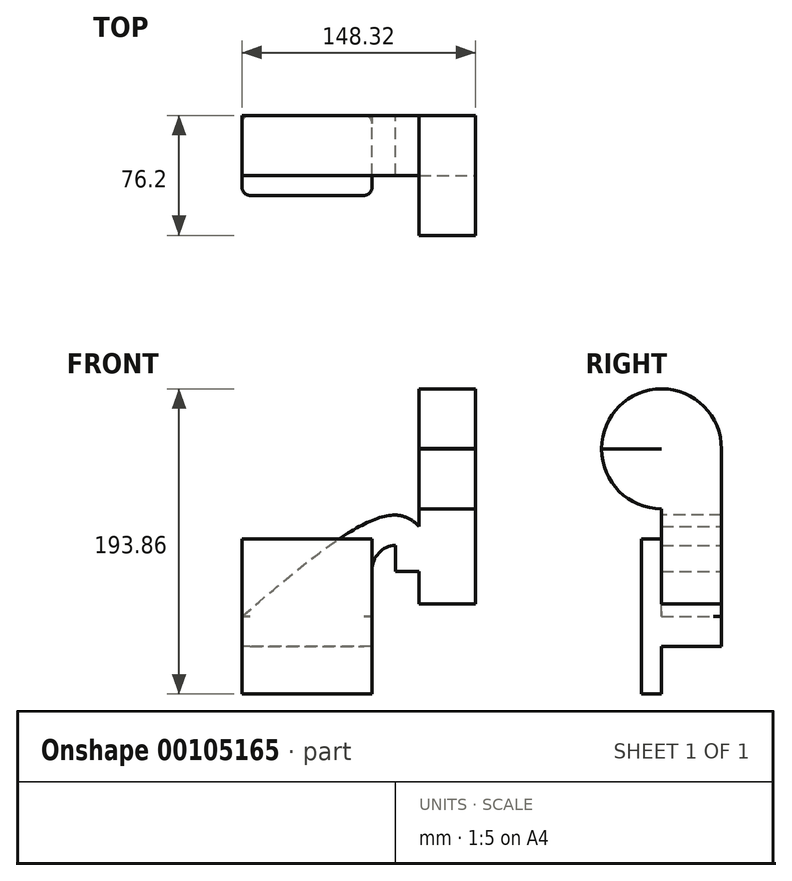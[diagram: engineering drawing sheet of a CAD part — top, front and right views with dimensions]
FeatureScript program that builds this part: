
annotation { "Feature Type Name" : "Feature", "Feature Type Description" : "" }
export const myFeature = defineFeature(function(context is Context, id is Id, definition is map)
    precondition{}
    {
        {
            var Q0;
            Q0=qCreatedBy(makeId("Front.planeOp"),FACE);
            var sketch = newSketch(context, id + "F0", { "sketchPlane" : qUnion([Q0])});
            skLineSegment(sketch, "E0.bottom", {"start": v(-41.28, 9.52) * mm, "end": v(41.27, 9.53) * mm});
            skLineSegment(sketch, "E0.top", {"start": v(-41.28, -9.53) * mm, "end": v(41.28, -9.53) * mm});
            skLineSegment(sketch, "E0.left", {"start": v(-41.28, 9.52) * mm, "end": v(-41.27, -9.53) * mm});
            skLineSegment(sketch, "E0.right", {"start": v(41.28, 9.53) * mm, "end": v(41.28, -9.52) * mm});
            skPoint(sketch, "E0.middle", {"position": v(0, 0) * mm});
            skLineSegment(sketch, "E1.bottom", {"start": v(56.24, 66.67) * mm, "end": v(107.04, 66.67) * mm});
            skLineSegment(sketch, "E1.top", {"start": v(56.24, 38.1) * mm, "end": v(107.04, 38.1) * mm});
            skLineSegment(sketch, "E1.left", {"start": v(56.24, 66.67) * mm, "end": v(56.24, 38.1) * mm});
            skLineSegment(sketch, "E1.right", {"start": v(107.04, 66.67) * mm, "end": v(107.04, 38.1) * mm});
            skPoint(sketch, "E1.middle", {"position": v(81.64, 52.39) * mm});
            skLineSegment(sketch, "E2", {"start": v(41.27, 9.53) * mm, "end": v(41.27, 38.94) * mm});
            skArc(sketch, "E3", {"start": v(41.27, 38.94) * mm, "mid": v(45.92, 50.17) * mm, "end": v(57.15, 54.81) * mm});
            skLineSegment(sketch, "E4", {"start": v(57.15, 54.81) * mm, "end": v(101.6, 54.81) * mm});
            skArc(sketch, "E5.0", {"start": v(22.22, 38.94) * mm, "mid": v(32.45, 63.64) * mm, "end": v(57.15, 73.86) * mm});
            skLineSegment(sketch, "E5.1", {"start": v(22.22, 9.53) * mm, "end": v(22.22, 38.94) * mm});
            skLineSegment(sketch, "E6", {"start": v(57.15, 54.81) * mm, "end": v(57.15, 73.86) * mm});
            skFitSpline(sketch, "E7", {"points": [v(-41.28, 9.52) * mm, v(57.15, 73.86) * mm, v(81.64, 52.39) * mm], "startDerivative": vector(176.18, 150.78) * mm, "endDerivative": vector(57.36, -89.95) * mm});
            skSolve(sketch);
        }
        {
            var Q0;
            Q0=makeQuery(id+"F0.imprint","IMPRINT",FACE,{"disambiguationData":[TD([[makeQuery(id+"F0.imprint","IMPRINT",EDGE,{"derivedFrom":sQuery(id+"F0.wireOp",EDGE,"E0.top")}),1.0]])]});
            extrude(context, id + "F1", {"entities" : qUnion([Q0]), "endBound" : BoundingType.SYMMETRIC, "depth" : 50.8 * mm});
        }
        {
            var Q0;
            Q0 = qSketchRegion(id + "F0", true);
            extrude(context, id + "F2", {"entities" : qUnion([Q0]), "operationType" : NewBodyOperationType.ADD, "endBound" : BoundingType.SYMMETRIC, "depth" : 25.4 * mm});
        }
        {
            var Q0;
            Q0=makeQuery(id+"F1.opExtrude","CAP_EDGE",EDGE,{"disambiguationData":[OSD([sQuery(id+"F0.wireOp",EDGE,"E0.right")])],"isStart":false});
            var Q1;
            Q1=makeQuery(id+"F1.opExtrude","CAP_EDGE",EDGE,{"disambiguationData":[OSD([sQuery(id+"F0.wireOp",EDGE,"E0.left")])],"isStart":false});
            fillet(context, id + "F3", {"entities" : qUnion([Q0, Q1]), "radius" : 5.08 * mm, "tangentPropagation" : true, "allowEdgeOverflow" : false});
        }
        {
            var Q0;
            Q0=makeQuery(id+"F1.opExtrude","CAP_EDGE",EDGE,{"disambiguationData":[OSD([sQuery(id+"F0.wireOp",EDGE,"E0.right")])],"isStart":true});
            var Q1;
            Q1=makeQuery(id+"F1.opExtrude","CAP_EDGE",EDGE,{"disambiguationData":[OSD([sQuery(id+"F0.wireOp",EDGE,"E0.left")])],"isStart":true});
            fillet(context, id + "F4", {"entities" : qUnion([Q0, Q1]), "radius" : 5.08 * mm, "tangentPropagation" : true, "allowEdgeOverflow" : false});
        }
        {
            var Q0;
            Q0=makeQuery(id+"F2.opExtrude","CAP_FACE",FACE,{"disambiguationData":[OSD([sQuery(id+"F0.wireOp",EDGE,"E0.top"),sQuery(id+"F0.wireOp",EDGE,"E0.left"),sQuery(id+"F0.wireOp",EDGE,"E0.right"),sQuery(id+"F0.wireOp",EDGE,"E1.bottom"),sQuery(id+"F0.wireOp",EDGE,"E1.top"),sQuery(id+"F0.wireOp",EDGE,"E1.left"),sQuery(id+"F0.wireOp",EDGE,"E1.right"),sQuery(id+"F0.wireOp",EDGE,"E2"),sQuery(id+"F0.wireOp",EDGE,"E3"),sQuery(id+"F0.wireOp",EDGE,"E7")])],"isStart":true});
            extrude(context, id + "F5", {"entities" : qUnion([Q0]), "operationType" : NewBodyOperationType.ADD, "endBound" : BoundingType.SYMMETRIC, "depth" : 25.4 * mm});
        }
        {
            var Q0;
            {var subQ0=sQuery(id+"F0.wireOp",EDGE,"E1.bottom");Q0=makeQuery(id+"F5.boolean.opBoolean","MERGE",FACE,{"derivedFrom":[makeQuery(id+"F2.opExtrude","SWEPT_FACE",FACE,{"disambiguationData":[OSD([subQ0])]}),makeQuery(id+"F5.opExtrude","SWEPT_FACE",FACE,{"disambiguationData":[OSD([subQ0])]})]});}
            var Q1;
            {var subQ2=sQuery(id+"F0.wireOp",EDGE,"E0.right");var subQ3=sQuery(id+"F0.wireOp",EDGE,"E0.left");var subQ4=sQuery(id+"F0.wireOp",EDGE,"E0.top");var subQ5=sQuery(id+"F0.wireOp",EDGE,"E0.bottom");Q1=makeQuery(id+"F2.boolean.opBoolean","SPLIT",FACE,{"disambiguationData":[TD([makeQuery(id+"F1.opExtrude","CAP_FACE",FACE,{"disambiguationData":[OSD([subQ5,subQ4,subQ3,subQ2])],"isStart":false})])],"derivedFrom":makeQuery(id+"F1.opExtrude","SWEPT_FACE",FACE,{"disambiguationData":[OSD([subQ5])]})});}
            extrude(context, id + "F6", {"entities" : qUnion([Q0, Q1]), "operationType" : NewBodyOperationType.ADD, "endBound" : BoundingType.SYMMETRIC, "depth" : 98.6 * mm});
        }
        {
            var Q0;
            Q0=makeQuery(id+"F6.opExtrude","CAP_FACE",FACE,{"disambiguationData":[OSD([sQuery(id+"F0.wireOp",EDGE,"E1.bottom")])],"isStart":false});
            var Q1;
            {var subQ0=sQuery(id+"F0.wireOp",EDGE,"E1.bottom");Q1=makeQuery(id+"F6.opExtrude","CAP_EDGE",EDGE,{"disambiguationData":[OSD([subQ0]),TDD([makeQuery(id+"F2.opExtrude","CAP_EDGE",EDGE,{"disambiguationData":[OSD([subQ0])],"isStart":false})])],"isStart":false});}
            revolve(context, id + "F7", {"operationType" : NewBodyOperationType.ADD, "entities" : qUnion([Q0]), "axis" : qUnion([Q1]), "revolveType" : RevolveType.SYMMETRIC, "oppositeDirection" : true, "angle" : 359.53 * degree});
        }
    });
